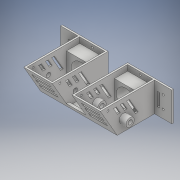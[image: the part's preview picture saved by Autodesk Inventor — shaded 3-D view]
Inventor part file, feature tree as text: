
AUTODESK INVENTOR PART (.ipt)
format: ipt  version: 2018.2 (Build 222227000, 227)  size: 453,120 bytes
history: native  units: mm
features: extrude x25, sketch x25, plane x1
ambient origin geometry x8: Origin, YZ Plane, XZ Plane, XY Plane, X Axis, Y Axis, Z Axis, Center Point
bodies: Solid1 (feature_tree)
feature tree (51):
  extrude  "Extrusion1"  Depth=56.0mm
  extrude  "Extrusion2"  Depth=2.4mm
  extrude  "Extrusion3"  Depth=2.4mm
  extrude  "Extrusion4"  Depth=2.4mm
  sketch  "Sketch5"  dims[d9=2.4mm d10=39.6mm d11=0.0mm]
  extrude  "Extrusion5"  Depth=39.6mm TaperAngle=0.0deg
  extrude  "Extrusion6"  Depth=14.0mm
  extrude  "Extrusion7"  Depth=2.4mm
  extrude  "Extrusion8"  Depth=39.6mm TaperAngle=0.0deg
  extrude  "Extrusion9"  Depth=3.0mm
  extrude  "Extrusion10"  Depth=12.0mm
  extrude  "Extrusion11"  Depth=19.0mm
  extrude  "Extrusion12"  Depth=17.0mm
  extrude  "Extrusion13"  Depth=12.0mm
  extrude  "Extrusion21"  Depth=12.0mm
  extrude  "Extrusion22"  Depth=12.0mm
  extrude  "Extrusion23"  Depth=12.0mm
  extrude  "Extrusion24"  Depth=8.0mm
  extrude  "Extrusion25"  Depth=16.0mm
  extrude  "Extrusion26"  Depth=25.0mm
  extrude  "Extrusion27"  Depth=23.0mm TaperAngle=0.0deg
  extrude  "Extrusion28"  Depth=3.0mm
  extrude  "Extrusion29"  Depth=12.5mm
  extrude  "Extrusion30"  Depth=20.0mm TaperAngle=0.0deg
  extrude  "Extrusion31"  Depth=3.0mm
  plane  "Work Plane1"
  extrude  "Extrusion32"  Depth=6.5mm
  sketch  "Sketch1"  dims[d0=110.0mm d1=56.0mm]
  sketch  "Sketch2"  dims[d2=25.0mm d3=2.4mm]
  sketch  "Sketch3"  dims[d4=25.0mm d5=2.4mm]
  sketch  "Sketch4"  dims[d6=42.0mm d7=0.0mm d8=2.4mm]
  sketch  "Sketch6"  dims[d12=14.0mm d13=14.0mm]
  sketch  "Sketch7"  dims[d14=39.6mm d15=0.0mm d16=2.4mm]
  sketch  "Sketch8"  dims[d17=2.4mm d18=39.6mm d19=0.0mm]
  sketch  "Sketch9"  dims[d20=3.0mm d21=3.0mm]
  sketch  "Sketch10"  dims[d22=12.0mm d23=12.0mm]
  sketch  "Sketch11"  dims[d24=19.0mm d25=0.0mm d26=6.3mm]
  sketch  "Sketch12"  dims[d27=17.0mm d28=45.0mm]
  sketch  "Sketch13"  dims[d29=110.0mm d30=0.0mm d31=12.0mm]
  sketch  "Sketch21"  dims[d32=10.0mm d33=0.0mm d34=12.0mm]
  sketch  "Sketch22"  dims[d35=8.0mm d36=0.0mm d37=12.0mm]
  sketch  "Sketch23"  dims[d38=10.0mm d39=0.0mm d40=12.0mm]
  sketch  "Sketch24"  dims[d41=8.0mm d42=0.0mm d43=26.5mm]
  sketch  "Sketch25"  dims[d44=26.5mm d45=16.0mm]
  sketch  "Sketch26"  dims[d46=16.0mm d47=25.0mm]
  sketch  "Sketch27"  dims[d48=25.0mm d49=23.0mm d50=0.0mm]
  sketch  "Sketch28"  dims[d51=3.0mm d52=3.0mm]
  sketch  "Sketch29"  dims[d53=12.5mm d54=12.5mm]
  sketch  "Sketch31"  dims[d55=12.5mm d56=20.0mm d57=0.0mm]
  sketch  "Sketch32"  dims[d58=3.0mm d59=3.0mm]
  sketch  "Sketch33"  dims[d60=6.5mm d61=6.5mm d62=20.0mm d63=0.0mm d84=30.0deg d85=2.4mm d86=0.0mm d87=30.0deg d88=2.4mm d89=0.0mm d90=30.0deg d91=2.4mm d92=0.0mm d93=30.0deg d94=2.4mm d95=0.0mm d96=2.4mm d97=38.0mm d98=0.0mm d99=2.4mm d100=38.0mm d101=0.0mm d102=7.0mm d103=90.0deg d104=28.0mm d105=0.0mm d106=3.0mm d107=5.0mm d108=7.0mm d109=120.0mm d110=0.0mm d111=4.0mm d112=10.0mm d113=4.0mm d114=4.0mm d115=10.0mm d116=6.0mm d117=6.0mm d118=5.0mm d119=4.0mm d120=4.0mm d121=5.0mm d122=6.0mm d123=120.0mm d124=0.0mm d125=8.0mm d126=0.0mm d127=3.0mm d128=3.0mm d129=4.0mm d130=4.0mm d131=18.0mm d132=18.0mm d133=8.0mm d134=0.0mm d135=-80.0mm d136=25.0mm d137=4.0mm d138=4.0mm d139=4.0mm d140=5.0mm d141=5.0mm d142=9.0mm d143=25.0mm d144=4.0mm d145=25.0mm d146=4.0mm d147=25.0mm d148=4.0mm d149=5.0mm d150=5.0mm d151=8.0mm d152=9.0mm d153=9.0mm d154=20.0mm d155=0.0mm d156=36.2mm d157=36.2mm]
